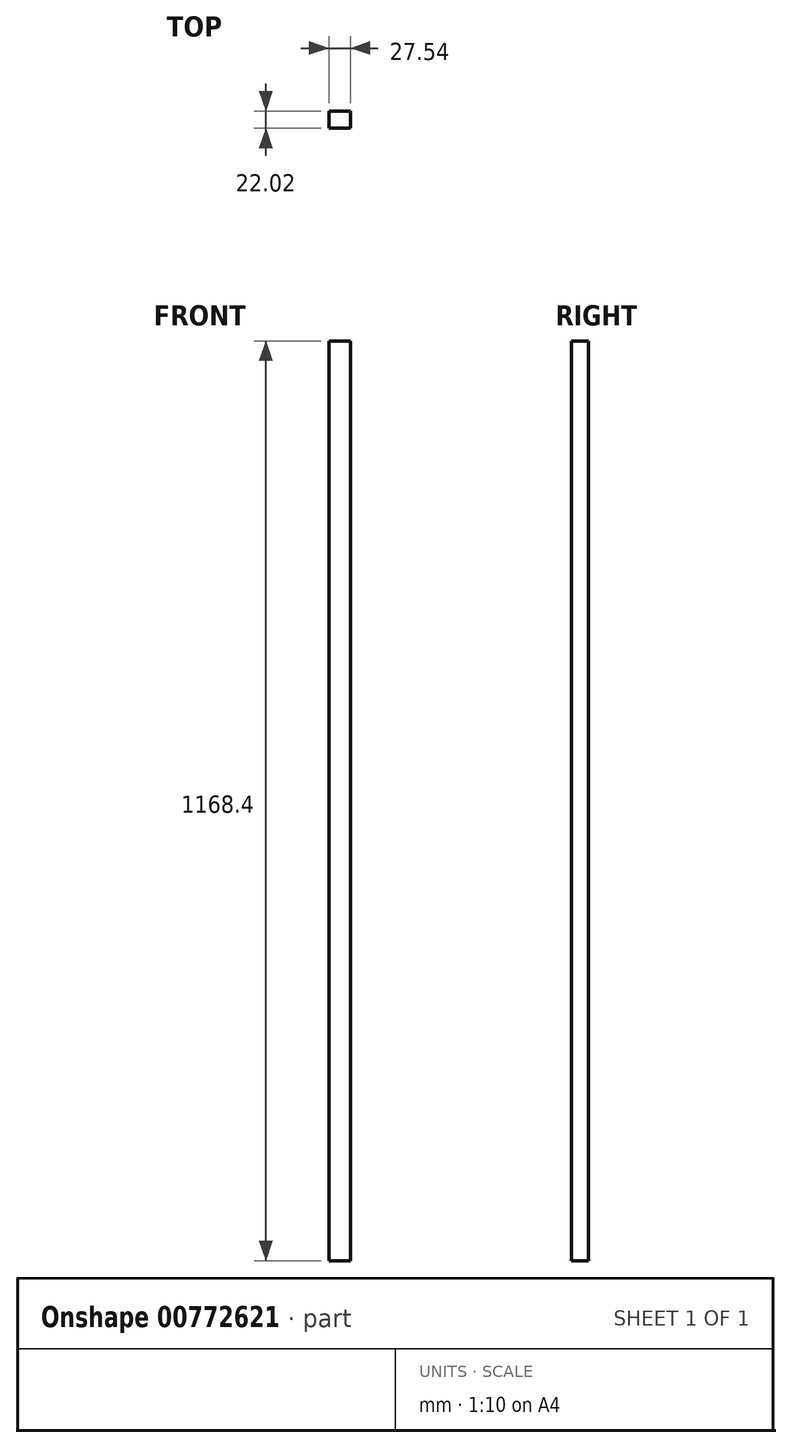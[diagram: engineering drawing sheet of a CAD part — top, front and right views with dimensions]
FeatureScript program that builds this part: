
annotation { "Feature Type Name" : "Feature", "Feature Type Description" : "" }
export const myFeature = defineFeature(function(context is Context, id is Id, definition is map)
    precondition{}
    {
        {
            var Q0;
            Q0=qCreatedBy(makeId("Top.planeOp"),FACE);
            var sketch = newSketch(context, id + "F0", { "sketchPlane" : qUnion([Q0])});
            skLineSegment(sketch, "E0.bottom", {"start": v(-13.77, 11.01) * mm, "end": v(13.77, 11.01) * mm});
            skLineSegment(sketch, "E0.top", {"start": v(-13.77, -11.01) * mm, "end": v(13.77, -11.01) * mm});
            skLineSegment(sketch, "E0.left", {"start": v(-13.77, 11.01) * mm, "end": v(-13.77, -11.01) * mm});
            skLineSegment(sketch, "E0.right", {"start": v(13.77, 11.01) * mm, "end": v(13.77, -11.01) * mm});
            skPoint(sketch, "E0.middle", {"position": v(0, 0) * mm});
            skSolve(sketch);
        }
        {
            var Q0;
            Q0=makeQuery(id+"F0.imprint","IMPRINT",FACE,{"disambiguationData":[TD([[makeQuery(id+"F0.imprint","IMPRINT",EDGE,{"derivedFrom":sQuery(id+"F0.wireOp",EDGE,"E0.bottom")}),-1.0]])]});
            extrude(context, id + "F1", {"entities" : qUnion([Q0]), "depth" : 1168.4 * mm, "offsetDistance" : 25.4 * mm});
        }
    });
